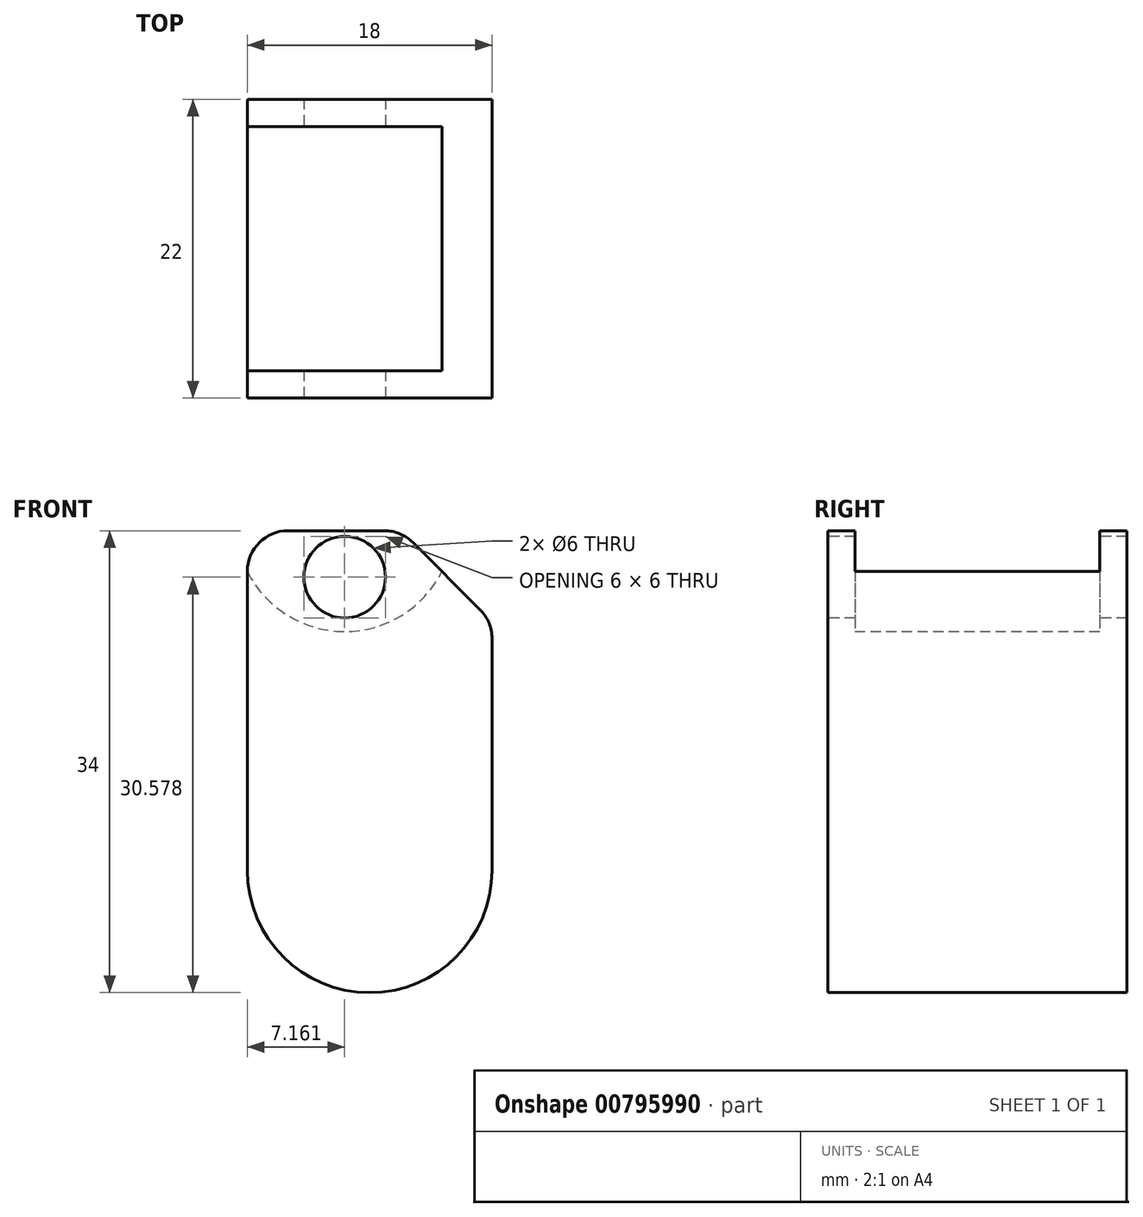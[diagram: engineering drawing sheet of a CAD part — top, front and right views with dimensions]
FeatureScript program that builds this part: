
annotation { "Feature Type Name" : "Feature", "Feature Type Description" : "" }
export const myFeature = defineFeature(function(context is Context, id is Id, definition is map)
    precondition{}
    {
        {
            var Q0;
            Q0=qCreatedBy(makeId("Front.planeOp"),FACE);
            var sketch = newSketch(context, id + "F0", { "sketchPlane" : qUnion([Q0])});
            skLineSegment(sketch, "E0", {"start": v(18, 0) * mm, "end": v(18, 18.31) * mm});
            skArc(sketch, "E1", {"start": v(0, 0) * mm, "mid": v(9, -9) * mm, "end": v(18, 0) * mm});
            skLineSegment(sketch, "E2", {"start": v(11.31, 25) * mm, "end": v(0, 25) * mm});
            skLineSegment(sketch, "E3", {"start": v(0, 25) * mm, "end": v(0, 0) * mm});
            skLineSegment(sketch, "E4", {"start": v(11.31, 25) * mm, "end": v(18, 18.31) * mm});
            skSolve(sketch);
        }
        {
            var Q0;
            Q0=makeQuery(id+"F0.imprint","IMPRINT",FACE,{"disambiguationData":[TD([[makeQuery(id+"F0.imprint","IMPRINT",EDGE,{"derivedFrom":sQuery(id+"F0.wireOp",EDGE,"E0")}),1.0]])]});
            extrude(context, id + "F1", {"entities" : qUnion([Q0]), "depth" : 22 * mm, "offsetDistance" : 25 * mm});
        }
        {
            var Q0;
            Q0=makeQuery(id+"F1.opExtrude","SWEPT_FACE",FACE,{"disambiguationData":[OSD([sQuery(id+"F0.wireOp",EDGE,"E3")])]});
            var sketch = newSketch(context, id + "F2", { "sketchPlane" : qUnion([Q0])});
            skLineSegment(sketch, "E5.bottom", {"start": v(2, 25) * mm, "end": v(20, 25) * mm});
            skLineSegment(sketch, "E5.top", {"start": v(2, 22) * mm, "end": v(20, 22) * mm});
            skLineSegment(sketch, "E5.left", {"start": v(2, 25) * mm, "end": v(2, 22) * mm});
            skLineSegment(sketch, "E5.right", {"start": v(20, 25) * mm, "end": v(20, 22) * mm});
            skSolve(sketch);
        }
        {
            var Q0;
            Q0=makeQuery(id+"F2.imprint","IMPRINT",FACE,{"disambiguationData":[TD([[makeQuery(id+"F2.imprint","IMPRINT",EDGE,{"derivedFrom":sQuery(id+"F2.wireOp",EDGE,"E5.bottom")}),1.0]])]});
            extrude(context, id + "F3", {"entities" : qUnion([Q0]), "operationType" : NewBodyOperationType.REMOVE, "oppositeDirection" : true, "depth" : 25 * mm, "offsetDistance" : 25 * mm});
        }
        {
            var Q0;
            Q0=qCreatedBy(makeId("Front.planeOp"),FACE);
            cPlane(context, id + "F4", {"entities" : qUnion([Q0]), "cplaneType" : CPlaneType.OFFSET, "offset" : 2 * mm, "width" : 150 * mm, "height" : 150 * mm});
        }
        {
            var Q0;
            Q0=qCreatedBy(id+"F4.planeOp",FACE);
            var sketch = newSketch(context, id + "F5", { "sketchPlane" : qUnion([Q0])});
            skPoint(sketch, "E6.0", {"position": v(0, 22) * mm});
            skPoint(sketch, "E7.0", {"position": v(14.31, 22) * mm});
            skPoint(sketch, "E8.0", {"position": v(18, 18.31) * mm});
            skLineSegment(sketch, "E9", {"start": v(0, 22) * mm, "end": v(14.31, 22) * mm});
            skLineSegment(sketch, "E10", {"start": v(14.31, 22) * mm, "end": v(18, 18.31) * mm});
            skArc(sketch, "E11", {"start": v(0, 22) * mm, "mid": v(7.16, 17.58) * mm, "end": v(14.31, 22) * mm});
            skSolve(sketch);
        }
        {
            var Q0;
            Q0 = qSketchRegion(id + "F5", true);
            extrude(context, id + "F6", {"entities" : qUnion([Q0]), "operationType" : NewBodyOperationType.REMOVE, "depth" : 18 * mm, "offsetDistance" : 25 * mm});
        }
        {
            var Q0;
            {var subQ0=sQuery(id+"F0.wireOp",EDGE,"E4");var subQ1=sQuery(id+"F0.wireOp",EDGE,"E0");Q0=makeQuery(id+"F6.boolean.opBoolean","SPLIT",EDGE,{"disambiguationData":[TD([makeQuery(id+"F3.boolean.opBoolean","COPY",FACE,{"derivedFrom":makeQuery(id+"F3.opExtrude","SWEPT_FACE",FACE,{"disambiguationData":[OSD([sQuery(id+"F2.wireOp",EDGE,"E5.right")])]})})])],"derivedFrom":makeQuery(id+"F1.opExtrude","SWEPT_EDGE",EDGE,{"disambiguationData":[OSD([subQ1,subQ0])]})});}
            var Q1;
            {var subQ0=sQuery(id+"F0.wireOp",EDGE,"E4");var subQ1=sQuery(id+"F0.wireOp",EDGE,"E0");Q1=makeQuery(id+"F6.boolean.opBoolean","SPLIT",EDGE,{"disambiguationData":[TD([makeQuery(id+"F3.boolean.opBoolean","COPY",FACE,{"derivedFrom":makeQuery(id+"F3.opExtrude","SWEPT_FACE",FACE,{"disambiguationData":[OSD([sQuery(id+"F2.wireOp",EDGE,"E5.left")])]})})])],"derivedFrom":makeQuery(id+"F1.opExtrude","SWEPT_EDGE",EDGE,{"disambiguationData":[OSD([subQ1,subQ0])]})});}
            var Q2;
            {var subQ0=sQuery(id+"F0.wireOp",EDGE,"E4");var subQ1=sQuery(id+"F0.wireOp",EDGE,"E2");Q2=makeQuery(id+"F3.boolean.opBoolean","SPLIT",EDGE,{"disambiguationData":[TD([makeQuery(id+"F3.opExtrude","SWEPT_FACE",FACE,{"disambiguationData":[OSD([sQuery(id+"F2.wireOp",EDGE,"E5.right")])]})])],"derivedFrom":makeQuery(id+"F1.opExtrude","SWEPT_EDGE",EDGE,{"disambiguationData":[OSD([subQ1,subQ0])]})});}
            var Q3;
            {var subQ0=sQuery(id+"F0.wireOp",EDGE,"E4");var subQ1=sQuery(id+"F0.wireOp",EDGE,"E2");Q3=makeQuery(id+"F3.boolean.opBoolean","SPLIT",EDGE,{"disambiguationData":[TD([makeQuery(id+"F3.opExtrude","SWEPT_FACE",FACE,{"disambiguationData":[OSD([sQuery(id+"F2.wireOp",EDGE,"E5.left")])]})])],"derivedFrom":makeQuery(id+"F1.opExtrude","SWEPT_EDGE",EDGE,{"disambiguationData":[OSD([subQ1,subQ0])]})});}
            var Q4;
            {var subQ0=sQuery(id+"F0.wireOp",EDGE,"E3");var subQ1=sQuery(id+"F0.wireOp",EDGE,"E2");Q4=makeQuery(id+"F3.boolean.opBoolean","SPLIT",EDGE,{"disambiguationData":[TD([makeQuery(id+"F3.opExtrude","SWEPT_FACE",FACE,{"disambiguationData":[OSD([sQuery(id+"F2.wireOp",EDGE,"E5.left")])]})])],"derivedFrom":makeQuery(id+"F1.opExtrude","SWEPT_EDGE",EDGE,{"disambiguationData":[OSD([subQ1,subQ0])]})});}
            var Q5;
            {var subQ0=sQuery(id+"F0.wireOp",EDGE,"E3");var subQ1=sQuery(id+"F0.wireOp",EDGE,"E2");Q5=makeQuery(id+"F3.boolean.opBoolean","SPLIT",EDGE,{"disambiguationData":[TD([makeQuery(id+"F3.opExtrude","SWEPT_FACE",FACE,{"disambiguationData":[OSD([sQuery(id+"F2.wireOp",EDGE,"E5.right")])]})])],"derivedFrom":makeQuery(id+"F1.opExtrude","SWEPT_EDGE",EDGE,{"disambiguationData":[OSD([subQ1,subQ0])]})});}
            fillet(context, id + "F7", {"entities" : qUnion([Q0, Q1, Q2, Q3, Q4, Q5]), "radius" : 3 * mm, "tangentPropagation" : true, "allowEdgeOverflow" : false});
        }
        {
            var Q0;
            Q0=makeQuery(id+"F1.opExtrude","CAP_FACE",FACE,{"disambiguationData":[OSD([sQuery(id+"F0.wireOp",EDGE,"E0"),sQuery(id+"F0.wireOp",EDGE,"E1"),sQuery(id+"F0.wireOp",EDGE,"E2"),sQuery(id+"F0.wireOp",EDGE,"E3"),sQuery(id+"F0.wireOp",EDGE,"E4")])],"isStart":false});
            var sketch = newSketch(context, id + "F8", { "sketchPlane" : qUnion([Q0])});
            skCircle(sketch, "E12", {"center": v(7.16, 21.58) * mm, "radius": 3 * mm});
            skPoint(sketch, "E13.0", {"position": v(7.16, 17.58) * mm});
            skArc(sketch, "E14.0", {"start": v(0, 22) * mm, "mid": v(7.16, 17.58) * mm, "end": v(14.31, 22) * mm});
            skSolve(sketch);
        }
        {
            var Q0;
            Q0=makeQuery(id+"F8.imprint","IMPRINT",FACE,{"disambiguationData":[TD([[makeQuery(id+"F8.imprint","IMPRINT",EDGE,{"derivedFrom":sQuery(id+"F8.wireOp",EDGE,"E12")}),1.0]])]});
            extrude(context, id + "F9", {"entities" : qUnion([Q0]), "operationType" : NewBodyOperationType.REMOVE, "oppositeDirection" : true, "depth" : 25 * mm, "offsetDistance" : 25 * mm});
        }
    });
